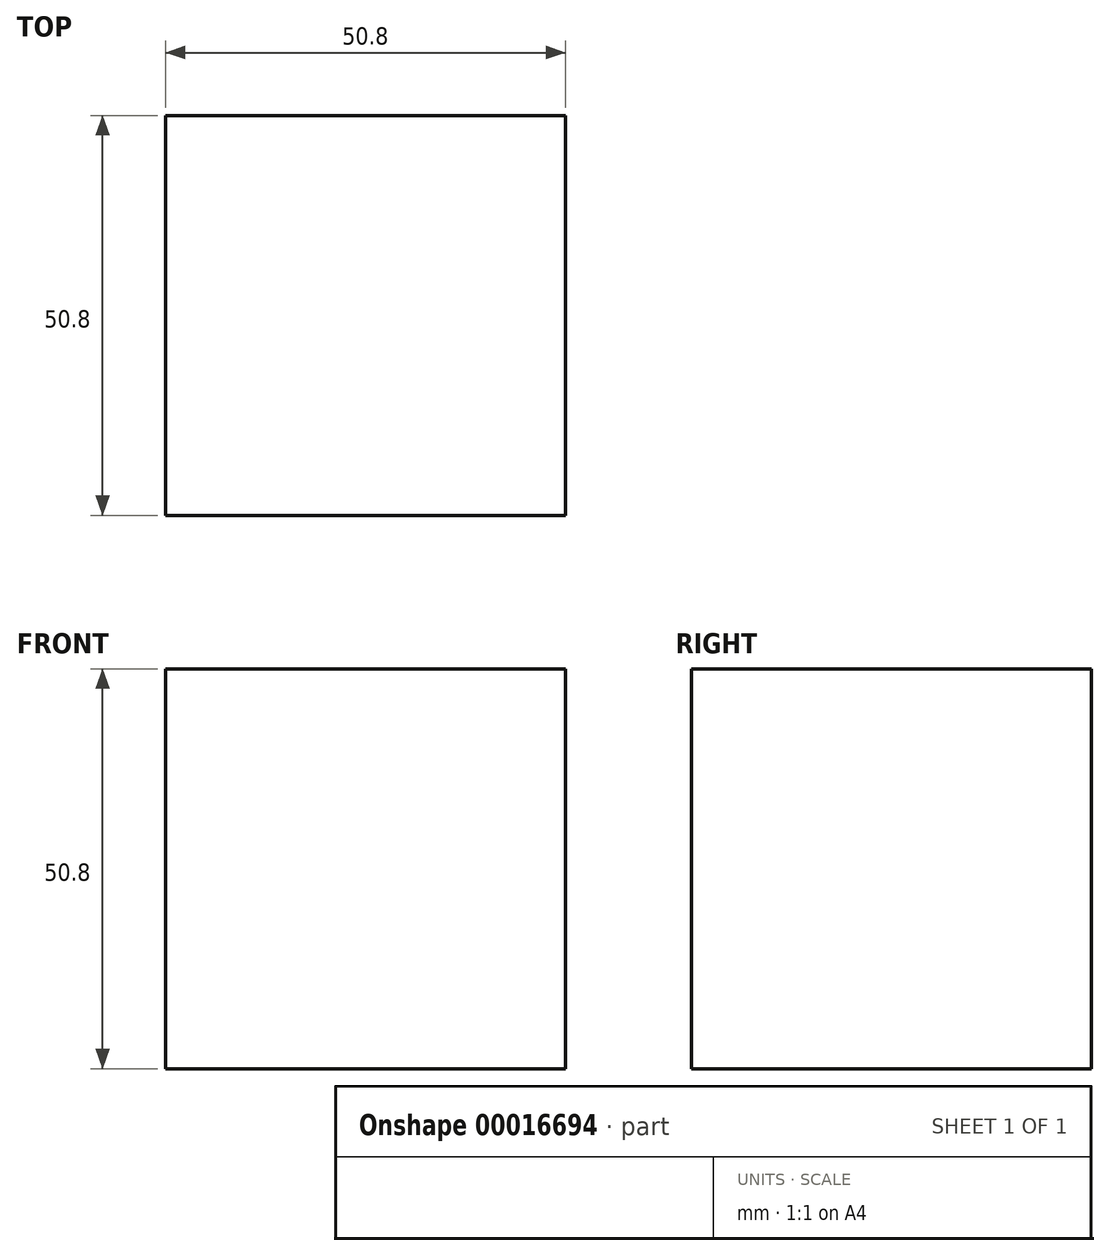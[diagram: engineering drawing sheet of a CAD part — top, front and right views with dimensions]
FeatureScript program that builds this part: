
annotation { "Feature Type Name" : "Feature", "Feature Type Description" : "" }
export const myFeature = defineFeature(function(context is Context, id is Id, definition is map)
    precondition{}
    {
        {
            var Q0;
            Q0=qCreatedBy(makeId("Top.planeOp"),FACE);
            var sketch = newSketch(context, id + "F0", { "sketchPlane" : qUnion([Q0])});
            skLineSegment(sketch, "E0.rect.bottom", {"start": v(25.4, 25.4) * mm, "end": v(-25.4, 25.4) * mm});
            skLineSegment(sketch, "E0.rect.top", {"start": v(25.4, -25.4) * mm, "end": v(-25.4, -25.4) * mm});
            skLineSegment(sketch, "E0.rect.left", {"start": v(25.4, 25.4) * mm, "end": v(25.4, -25.4) * mm});
            skLineSegment(sketch, "E0.rect.right", {"start": v(-25.4, 25.4) * mm, "end": v(-25.4, -25.4) * mm});
            skPoint(sketch, "E0.rect.middle", {"position": v(0, 0) * mm});
            skSolve(sketch);
        }
        {
            var Q0;
            Q0=makeQuery(id+"F0.imprint","IMPRINT",FACE,{"disambiguationData":[TD([[makeQuery(id+"F0.imprint","IMPRINT",EDGE,{"derivedFrom":sQuery(id+"F0.wireOp",EDGE,"E0.rect.bottom")}),1.0]])]});
            extrude(context, id + "F1", {"entities" : qUnion([Q0]), "depth" : 50.8 * mm});
        }
    });
